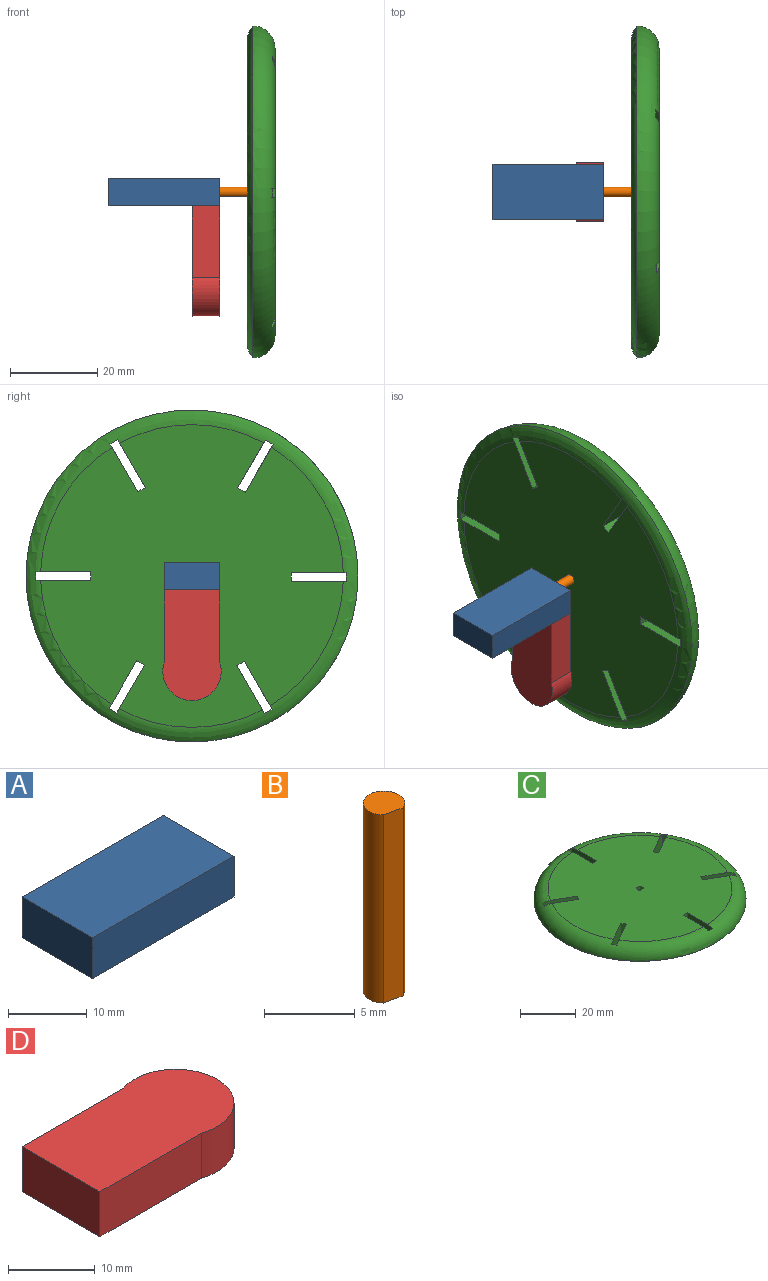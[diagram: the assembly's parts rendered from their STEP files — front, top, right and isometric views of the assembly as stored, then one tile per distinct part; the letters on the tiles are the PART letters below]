
ASSEMBLY  parts=4 mates=3
PART A: 6 faces, bbox 25.4x12.7x6.4 mm
  f0: plane 25.4x6.35mm, normal (0,-1,0), area 161.3mm2, adj f1,f3,f4,f5
  f1: plane 12.7x6.35mm, normal (1,0,0), area 80.6mm2, adj f0,f2,f4,f5
  f2: plane 25.4x6.35mm, normal (0,1,0), area 161.3mm2, adj f1,f3,f4,f5
  f3: plane 12.7x6.35mm, normal (-1,0,0), area 80.6mm2, adj f0,f2,f4,f5
  f4: plane 25.4x12.7mm, normal (0,0,1), area 322.6mm2, adj f0,f1,f2,f3
  f5: plane 25.4x12.7mm, normal (0,0,-1), area 322.6mm2, adj f0,f1,f2,f3
PART B: 4 faces, bbox 2.3x2.2x12.7 mm
  f0: plane 12.7x1.24mm, normal (-0.21,-0.98,0), area 16.1mm2, adj f1,f2,f3
  f1: cylinder r=1.14mm len=12.7mm, axis (0,0,-1), area 74.1mm2, adj f0,f2,f3
  f2: plane 2.29x2.2mm, normal (0,0,1), area 3.9mm2, adj f0,f1
  f3: plane 2.29x2.2mm, normal (0,0,-1), area 3.9mm2, adj f0,f1
PART C: 30 faces, bbox 83x83x6.4 mm
  f0: plane 11.01x6.36mm, normal (-0.5,-0.87,0), area 80mm2, adj f1,f25,f26,f27,f28,f29
  f1: plane 6.35x1.76mm, normal (-0.87,0.5,0), area 12.9mm2, adj f0,f2,f26,f27
  f2: plane 11.01x6.36mm, normal (0.5,0.87,0), area 80mm2, adj f1,f25,f26,f27,f28,f29
  f3: plane 11.01x6.36mm, normal (0.5,-0.87,0), area 80.1mm2, adj f4,f19,f26,f27,f28,f29
  f4: plane 6.35x1.76mm, normal (-0.87,-0.5,0), area 12.9mm2, adj f3,f5,f26,f27
  f5: plane 11.01x6.36mm, normal (-0.5,0.87,0), area 80.1mm2, adj f4,f19,f26,f27,f28,f29
  f6: plane 12.71x6.36mm, normal (1,0,0), area 80.1mm2, adj f7,f20,f26,f27,f28,f29
  f7: plane 6.35x2.03mm, normal (0,-1,0), area 12.9mm2, adj f6,f8,f26,f27
  f8: plane 12.71x6.36mm, normal (-1,0,0), area 80.1mm2, adj f7,f20,f26,f27,f28,f29
  f9: plane 11.01x6.36mm, normal (0.5,0.87,0), area 80mm2, adj f10,f21,f26,f27,f28,f29
  f10: plane 6.35x1.76mm, normal (0.87,-0.5,0), area 12.9mm2, adj f9,f11,f26,f27
  f11: plane 11.01x6.36mm, normal (-0.5,-0.87,0), area 80mm2, adj f10,f21,f26,f27,f28,f29
  f12: plane 11.01x6.36mm, normal (-0.5,0.87,0), area 79.8mm2, adj f13,f22,f26,f27,f28,f29
  f13: plane 6.35x1.76mm, normal (0.87,0.5,0), area 12.9mm2, adj f12,f14,f26,f27
  f14: plane 11.01x6.36mm, normal (0.5,-0.87,0), area 79.8mm2, adj f13,f22,f26,f27,f28,f29
  f15: plane 12.71x6.36mm, normal (-1,0,0), area 79.8mm2, adj f16,f23,f26,f27,f28,f29
  f16: plane 6.35x2.03mm, normal (0,1,0), area 12.9mm2, adj f15,f17,f26,f27
  f17: plane 12.71x6.36mm, normal (1,0,0), area 79.8mm2, adj f16,f23,f26,f27,f28,f29
  f18: cylinder r=1.14mm len=6.35mm, axis (0,0,-1), area 37.1mm2, adj f24,f26,f27
  f19: plane 5.72x1.79mm, normal (0.87,0.5,0), area 11.5mm2, adj f3,f5,f28,f29
  f20: plane 5.69x2.03mm, normal (0,1,0), area 11.5mm2, adj f6,f8,f28,f29
  f21: plane 5.52x1.76mm, normal (-0.87,0.5,0), area 11.2mm2, adj f9,f11,f28,f29
  f22: plane 5.34x1.76mm, normal (-0.87,-0.5,0), area 10.8mm2, adj f12,f14,f28,f29
  f23: plane 5.37x2.07mm, normal (0,-1,0), area 10.8mm2, adj f15,f17,f28,f29
  f24: plane 6.35x1.27mm, normal (0,1,0), area 8.1mm2, adj f18,f26,f27
  f25: plane 5.52x1.76mm, normal (0.87,-0.5,0), area 11.2mm2, adj f0,f2,f28,f29
  f26: plane 66.04x66.02mm, normal (0,0,1), area 3298.9mm2, adj f0,f1,f2,f3,f4,f5,f6,f7
  f27: plane 69.48x69.46mm, normal (0,0,-1), area 3644mm2, adj f0,f1,f2,f3,f4,f5,f6,f7
  f28: torus R=33.02mm, axis (0,0,1), area 1783.6mm2, adj f0,f2,f3,f5,f6,f8,f9,f11
  f29: torus R=34.74mm, axis (0,0,-1), area 830.5mm2, adj f0,f2,f3,f5,f6,f8,f9,f11
PART D: 6 faces, bbox 25.4x13.4x6.4 mm
  f0: cylinder r=6.71mm len=13.43mm, axis (0,0,-1), area 162.1mm2, adj f1,f3,f4,f5
  f1: plane 16.51x6.35mm, normal (0,1,0), area 104.8mm2, adj f0,f2,f4,f5
  f2: plane 12.7x6.35mm, normal (-1,0,0), area 80.6mm2, adj f1,f3,f4,f5
  f3: plane 16.51x6.35mm, normal (0,-1,0), area 104.8mm2, adj f0,f2,f4,f5
  f4: plane 25.4x13.43mm, normal (0,0,1), area 309.2mm2, adj f0,f1,f2,f3
  f5: plane 25.4x13.43mm, normal (0,0,-1), area 309.2mm2, adj f0,f1,f2,f3
PLACE A at identity
PLACE B rot(axis=(0.58,-0.58,-0.58),120deg) t=(12.7,-63.16,-55.04)mm
PLACE C rot(axis=(0,1,0),90deg) t=(6.35,6.35,3.17)mm
PLACE D rot(axis=(0.71,0,-0.71),180deg) t=(0,6.35,-13.85)mm
MATE revolute B.f1 <-> A.f1  axis (-1,0,0) through (0,6.35,3.17)mm
MATE fastened D.f2 <-> A.f5  axis (0,0,1) through (0,6.35,0)mm
MATE fastened C.f18 <-> B.f1  axis (1,0,0) through (12.7,6.35,3.17)mm
